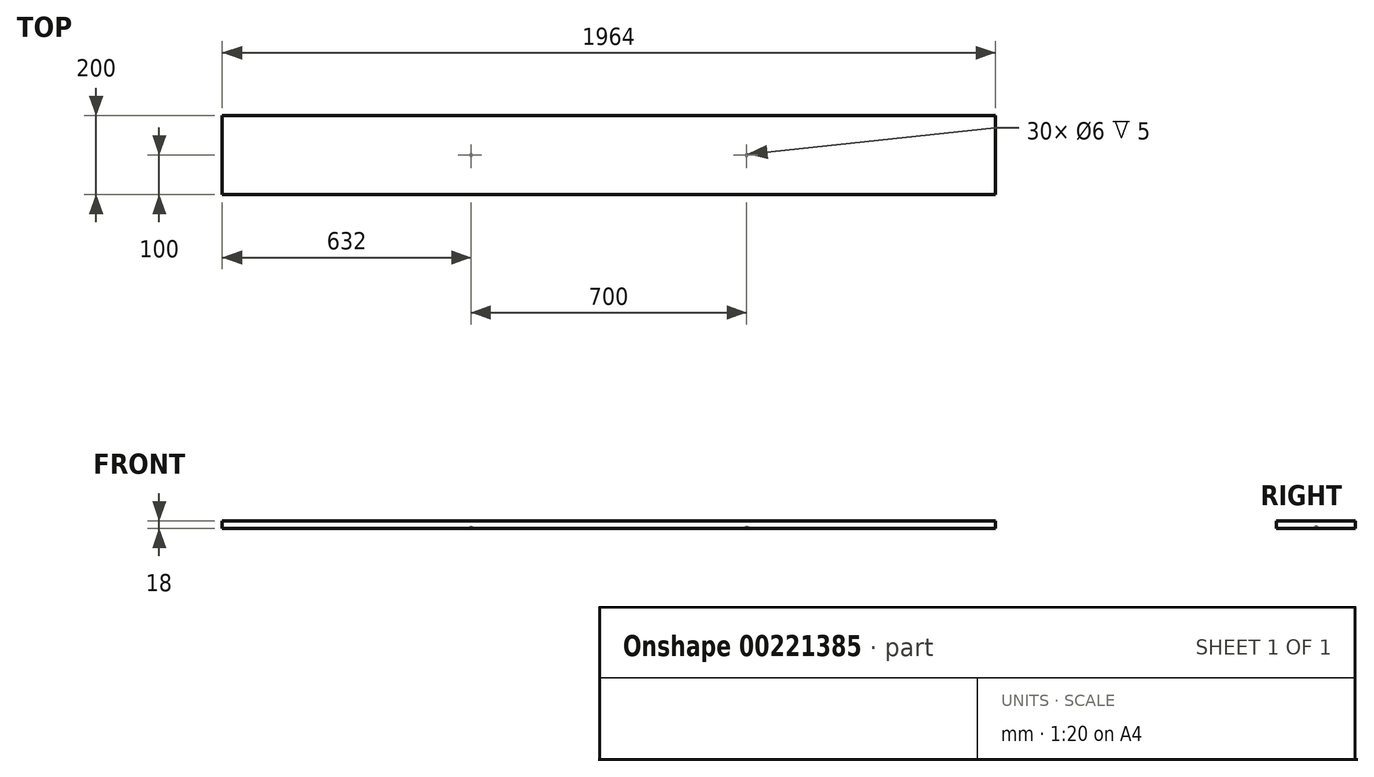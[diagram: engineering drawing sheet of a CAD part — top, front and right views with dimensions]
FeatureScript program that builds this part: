
annotation { "Feature Type Name" : "Feature", "Feature Type Description" : "" }
export const myFeature = defineFeature(function(context is Context, id is Id, definition is map)
    precondition{}
    {
        {
            var Q0;
            Q0=qCreatedBy(makeId("Top.planeOp"),FACE);
            var sketch = newSketch(context, id + "F0", { "sketchPlane" : qUnion([Q0])});
            skLineSegment(sketch, "E0.bottom", {"start": v(982, -100) * mm, "end": v(-982, -100) * mm});
            skLineSegment(sketch, "E0.top", {"start": v(982, 100) * mm, "end": v(-982, 100) * mm});
            skLineSegment(sketch, "E0.left", {"start": v(982, -100) * mm, "end": v(982, 100) * mm});
            skLineSegment(sketch, "E0.right", {"start": v(-982, -100) * mm, "end": v(-982, 100) * mm});
            skPoint(sketch, "E0.middle", {"position": v(0, 0) * mm});
            skSolve(sketch);
        }
        {
            var Q0;
            Q0 = qSketchRegion(id + "F0", true);
            extrude(context, id + "F1", {"entities" : qUnion([Q0]), "depth" : 18 * mm});
        }
        {
            var Q0;
            Q0=makeQuery(id+"F1.opExtrude","CAP_FACE",FACE,{"disambiguationData":[OSD([sQuery(id+"F0.wireOp",EDGE,"E0.bottom"),sQuery(id+"F0.wireOp",EDGE,"E0.top"),sQuery(id+"F0.wireOp",EDGE,"E0.left"),sQuery(id+"F0.wireOp",EDGE,"E0.right")])],"isStart":true});
            var sketch = newSketch(context, id + "F2", { "sketchPlane" : qUnion([Q0])});
            skCircle(sketch, "E1", {"center": v(-350, 0) * mm, "radius": 3 * mm});
            skCircle(sketch, "E2", {"center": v(350, 0) * mm, "radius": 3 * mm});
            skSolve(sketch);
        }
        {
            var Q0;
            Q0 = qSketchRegion(id + "F2", true);
            extrude(context, id + "F3", {"entities" : qUnion([Q0]), "operationType" : NewBodyOperationType.REMOVE, "oppositeDirection" : true, "depth" : 5 * mm});
        }
    });
